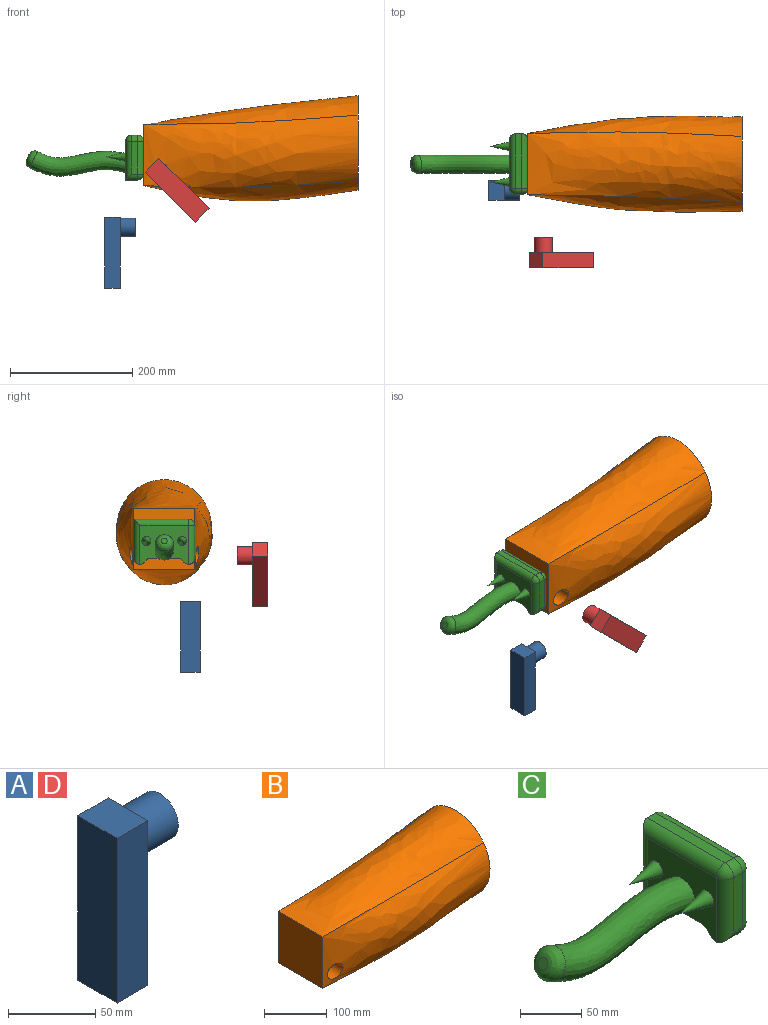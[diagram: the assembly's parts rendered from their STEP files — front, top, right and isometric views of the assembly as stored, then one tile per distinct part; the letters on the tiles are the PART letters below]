
ASSEMBLY  parts=4 mates=2
PART A: 8 faces, bbox 50x32x115.8 mm
  f0: plane 32.03x25mm, normal (0,0,-1), area 800.8mm2, adj f1,f3,f4,f5
  f1: plane 115.84x25mm, normal (0,1,0), area 2896.1mm2, adj f0,f2,f4,f5
  f2: plane 32.03x25mm, normal (0,0,1), area 800.8mm2, adj f1,f3,f4,f5
  f3: plane 115.84x25mm, normal (0,-1,0), area 2896.1mm2, adj f0,f2,f4,f5
  f4: plane 115.84x32.03mm, normal (1,0,0), area 3003.9mm2, adj f0,f1,f2,f3,f6
  f5: plane 115.84x32.03mm, normal (-1,0,0), area 3710.8mm2, adj f0,f1,f2,f3
  f6: cylinder r=15mm len=30mm, axis (-1,0,0), area 2356.2mm2, adj f4,f7
  f7: plane 30x30mm, normal (1,0,0), area 706.9mm2, adj f6
PART B: 7 faces, bbox 350x165.3x172.2 mm
  f0: plane 100x100mm, normal (-1,0,0), area 10000mm2, adj f2,f3,f4,f5
  f1: plane 154.39x154.39mm, normal (1,0,0), area 18706.8mm2, adj f2,f3,f4,f5
  f2: bspline ~350x115.09mm, area 40547.8mm2, adj f0,f1,f3,f5
  f3: bspline ~350x140.81mm, area 39767mm2, adj f0,f1,f2,f4,f6
  f4: bspline ~350x117.24mm, area 40570.8mm2, adj f0,f1,f3,f5
  f5: bspline ~350x120.51mm, area 39763mm2, adj f0,f1,f2,f4,f6
  f6: cylinder r=15mm len=112.9mm, axis (0,-1,0), area 10077.8mm2, adj f3,f5
PART C: 33 faces, bbox 203x99.6x82 mm
  f0: plane 79.61x53.79mm, normal (1,0,0), area 3598.6mm2, adj f13,f16,f17,f19,f20,f24,f27,f28
  f1: plane 53.79x10mm, normal (0,-1,0), area 537.9mm2, adj f26,f27,f31,f32
  f2: plane 20x3.12mm, normal (0,0.75,-0.66), area 83mm2, adj f7,f21,f28,f32
  f3: plane 44.04x20mm, normal (0,0,-1), area 880.9mm2, adj f7,f14,f20,f21
  f4: plane 20x3.12mm, normal (0,-0.75,-0.66), area 83mm2, adj f7,f13,f14,f18
  f5: plane 63.79x10mm, normal (0,1,0), area 637.9mm2, adj f6,f16,f18,f22
  f6: plane 89.61x10mm, normal (0,0,1), area 896.1mm2, adj f5,f19,f25,f26
  f7: plane 79.61x63.79mm, normal (-1,0,0), area 3395.5mm2, adj f2,f3,f4,f8,f10,f11,f14,f18
  f8: bspline ~192.01x73.15mm, area 14486.4mm2, adj f7,f12
  f9: plane 10x8.93mm, normal (-0.89,0,0.45), area 78.6mm2, adj f12
  f10: cone r=0mm half-angle=13.5deg, axis (1,0,0), area 732.5mm2, adj f7
  f11: cone r=0mm half-angle=13.5deg, axis (1,0,0), area 732.5mm2, adj f7
  f12: bspline ~31.23x30.01mm, area 1121.8mm2, adj f8,f9
  f13: cylinder r=10mm len=10.26mm, axis (0,-0.66,0.75), area 65.2mm2, adj f0,f4,f15,f17
  f14: cylinder r=10mm len=20mm, axis (-1,0,0), area 170.4mm2, adj f3,f4,f7,f17
  f15: sphere r=10mm, area 242.3mm2, adj f13,f16,f18
  f16: cylinder r=10mm len=63.79mm, axis (0,0,-1), area 944.9mm2, adj f0,f5,f15,f19
  f17: torus R=20mm, axis (1,0,0), area 182.5mm2, adj f0,f13,f14,f20
  f18: cylinder r=10mm len=20mm, axis (-1,0,0), area 427.5mm2, adj f4,f5,f7,f15,f22
  f19: cylinder r=10mm len=89.61mm, axis (0,1,0), area 1350.5mm2, adj f0,f6,f16,f23
  f20: cylinder r=10mm len=44.04mm, axis (0,-1,0), area 691.8mm2, adj f0,f3,f17,f24
  f21: cylinder r=10mm len=20mm, axis (1,0,0), area 170.4mm2, adj f2,f3,f7,f24
  f22: cylinder r=10mm len=73.79mm, axis (0,0,1), area 1044.9mm2, adj f5,f7,f18,f25
  f23: sphere r=10mm, area 157.1mm2, adj f19,f26,f27
  f24: torus R=20mm, axis (1,0,0), area 182.5mm2, adj f0,f20,f21,f28
  f25: cylinder r=10mm len=89.61mm, axis (0,-1,0), area 1350.5mm2, adj f6,f7,f22,f29
  f26: cylinder r=10mm len=10mm, axis (1,0,0), area 157.1mm2, adj f1,f6,f23,f29
  f27: cylinder r=10mm len=53.79mm, axis (0,0,1), area 844.9mm2, adj f0,f1,f23,f30
  f28: cylinder r=10mm len=10.26mm, axis (0,-0.66,-0.75), area 65.2mm2, adj f0,f2,f24,f30
  f29: sphere r=10mm, area 157.1mm2, adj f25,f26,f31
  f30: sphere r=10mm, area 242.3mm2, adj f27,f28,f32
  f31: cylinder r=10mm len=63.79mm, axis (0,0,-1), area 944.9mm2, adj f1,f7,f29,f32
  f32: cylinder r=10mm len=20mm, axis (-1,0,0), area 427.5mm2, adj f1,f2,f7,f30,f31
PART D: same geometry as A
PLACE A t=(-68.45,-83.07,-253.59)mm
PLACE B t=(-4.64,-24.35,-35.99)mm fixed
PLACE C t=(-34.64,-24.35,-38.89)mm
PLACE D rot(axis=(-0.36,-0.36,0.86),98.4deg) t=(101.92,-193.69,-123)mm
MATE slider C.f0 <-> B.f0  axis (1,0,0) through (-4.64,-24.35,-35.99)mm
MATE cylindrical D.f6 <-> B.f6  axis (0,-1,0) through (20.55,-156.19,-63.23)mm
